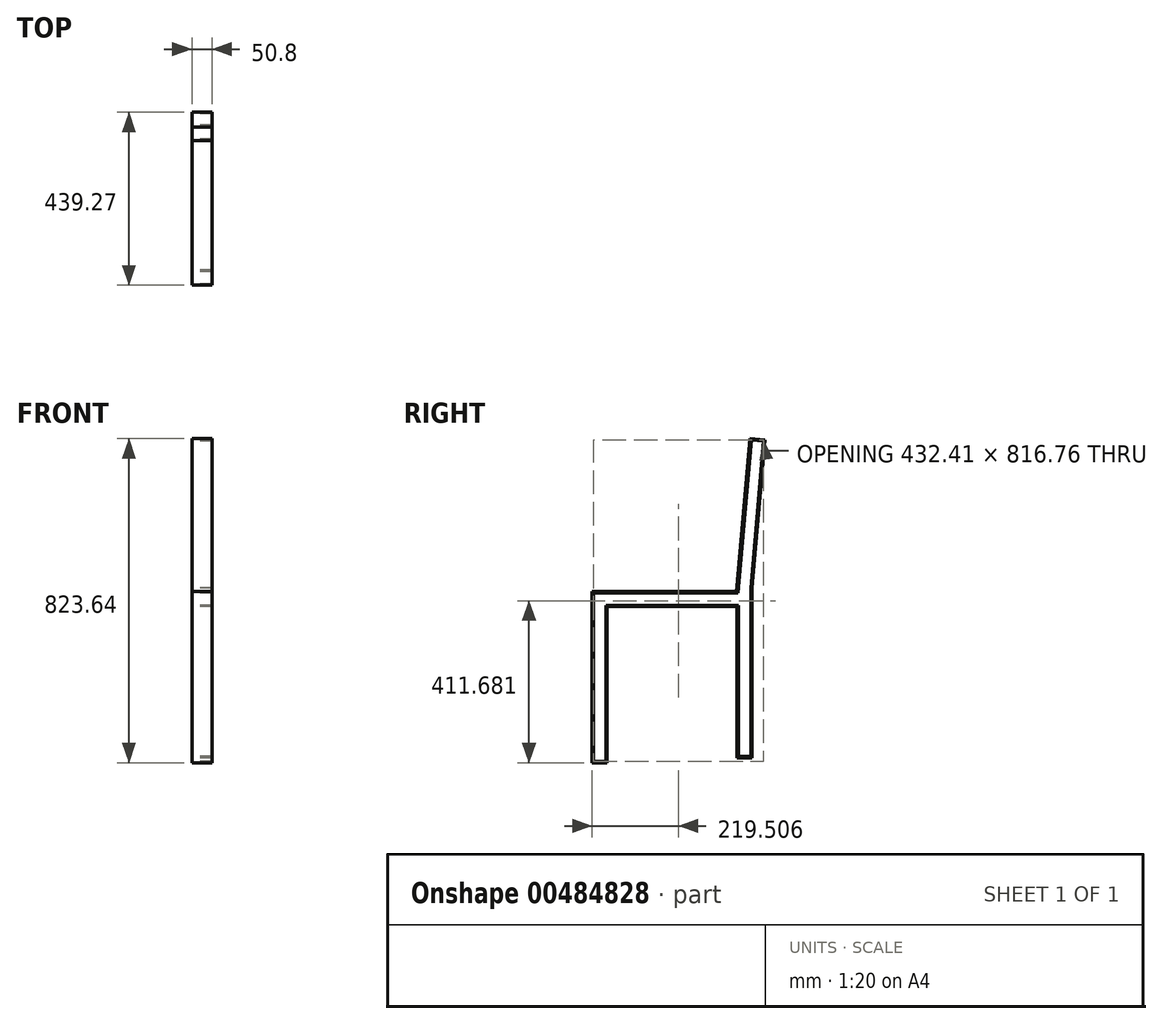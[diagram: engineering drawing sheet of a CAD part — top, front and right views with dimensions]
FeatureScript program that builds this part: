
annotation { "Feature Type Name" : "Feature", "Feature Type Description" : "" }
export const myFeature = defineFeature(function(context is Context, id is Id, definition is map)
    precondition{}
    {
        {
            var Q0;
            Q0=qCreatedBy(makeId("Right.planeOp"),FACE);
            var sketch = newSketch(context, id + "F0", { "sketchPlane" : qUnion([Q0])});
            skLineSegment(sketch, "E0.bottom", {"start": v(0, 0) * mm, "end": v(7.74, -12.7) * mm});
            skLineSegment(sketch, "E0.right", {"start": v(7.74, -12.7) * mm, "end": v(7.74, 419.1) * mm});
            skLineSegment(sketch, "E1.bottom", {"start": v(7.74, -12.7) * mm, "end": v(45.84, -12.7) * mm});
            skLineSegment(sketch, "E1.top", {"start": v(11.04, -9.4) * mm, "end": v(42.54, -9.4) * mm});
            skLineSegment(sketch, "E1.left", {"start": v(7.74, -12.7) * mm, "end": v(7.74, -9.4) * mm});
            skLineSegment(sketch, "E1.right", {"start": v(45.84, -12.7) * mm, "end": v(45.84, -9.4) * mm});
            skLineSegment(sketch, "E2.left", {"start": v(45.84, -9.4) * mm, "end": v(45.84, 384.3) * mm});
            skLineSegment(sketch, "E2.right", {"start": v(42.54, -9.4) * mm, "end": v(42.54, 384.3) * mm});
            skLineSegment(sketch, "E3.bottom", {"start": v(11.04, 419.1) * mm, "end": v(374.78, 419.1) * mm});
            skLineSegment(sketch, "E3.left", {"start": v(7.74, 419.1) * mm, "end": v(7.74, 422.4) * mm});
            skLineSegment(sketch, "E4.bottom", {"start": v(45.84, 384.3) * mm, "end": v(376.04, 384.3) * mm});
            skLineSegment(sketch, "E4.top", {"start": v(42.54, 387.6) * mm, "end": v(379.34, 387.6) * mm});
            skLineSegment(sketch, "E4.left", {"start": v(42.54, 384.3) * mm, "end": v(42.54, 387.6) * mm});
            skLineSegment(sketch, "E4.right", {"start": v(379.34, 384.3) * mm, "end": v(379.34, 387.6) * mm});
            skLineSegment(sketch, "E5.bottom", {"start": v(379.34, 387.6) * mm, "end": v(376.04, 387.6) * mm});
            skLineSegment(sketch, "E5.top", {"start": v(379.34, 0) * mm, "end": v(376.04, 0) * mm});
            skLineSegment(sketch, "E5.left", {"start": v(379.34, 387.6) * mm, "end": v(379.34, 3.3) * mm});
            skLineSegment(sketch, "E5.right", {"start": v(376.04, 384.3) * mm, "end": v(376.04, 0) * mm});
            skLineSegment(sketch, "E6.bottom", {"start": v(376.04, 0) * mm, "end": v(379.34, 0) * mm});
            skLineSegment(sketch, "E6.left", {"start": v(376.04, 0) * mm, "end": v(376.04, 4.83) * mm});
            skPoint(sketch, "E7.top.end.orphan", {"position": v(549.01, 387.6) * mm});
            skLineSegment(sketch, "E8.left", {"start": v(375.07, 422.4) * mm, "end": v(409.06, 810.94) * mm});
            skLineSegment(sketch, "E8.right", {"start": v(379.21, 431.9) * mm, "end": v(412.1, 807.75) * mm});
            skLineSegment(sketch, "E9", {"start": v(11.04, 419.1) * mm, "end": v(11.04, -9.4) * mm});
            skLineSegment(sketch, "E10", {"start": v(376.04, 0) * mm, "end": v(414.14, 0) * mm});
            skLineSegment(sketch, "E11", {"start": v(414.14, 0) * mm, "end": v(414.14, 431.9) * mm});
            skLineSegment(sketch, "E12", {"start": v(410.84, 431.9) * mm, "end": v(410.84, 3.3) * mm});
            skLineSegment(sketch, "E13", {"start": v(410.84, 3.3) * mm, "end": v(379.34, 3.3) * mm});
            skLineSegment(sketch, "E14", {"start": v(410.84, 431.9) * mm, "end": v(443.45, 804.62) * mm});
            skLineSegment(sketch, "E15", {"start": v(414.14, 431.9) * mm, "end": v(447.01, 807.62) * mm});
            skLineSegment(sketch, "E16", {"start": v(409.06, 810.94) * mm, "end": v(447.01, 807.62) * mm});
            skLineSegment(sketch, "E17", {"start": v(409.06, 810.94) * mm, "end": v(408.77, 807.65) * mm});
            skLineSegment(sketch, "E18", {"start": v(412.06, 807.36) * mm, "end": v(443.45, 804.62) * mm});
            skLineSegment(sketch, "E19", {"start": v(7.74, 422.4) * mm, "end": v(375.07, 422.4) * mm});
            skLineSegment(sketch, "E20", {"start": v(379.21, 431.9) * mm, "end": v(378.1, 419.1) * mm});
            skLineSegment(sketch, "E21", {"start": v(374.78, 419.1) * mm, "end": v(378.1, 419.1) * mm});
            skSolve(sketch);
        }
        {
            var Q0;
            Q0 = qSketchRegion(id + "F0", true);
            extrude(context, id + "F1", {"entities" : qUnion([Q0]), "depth" : 50.8 * mm});
        }
    });
